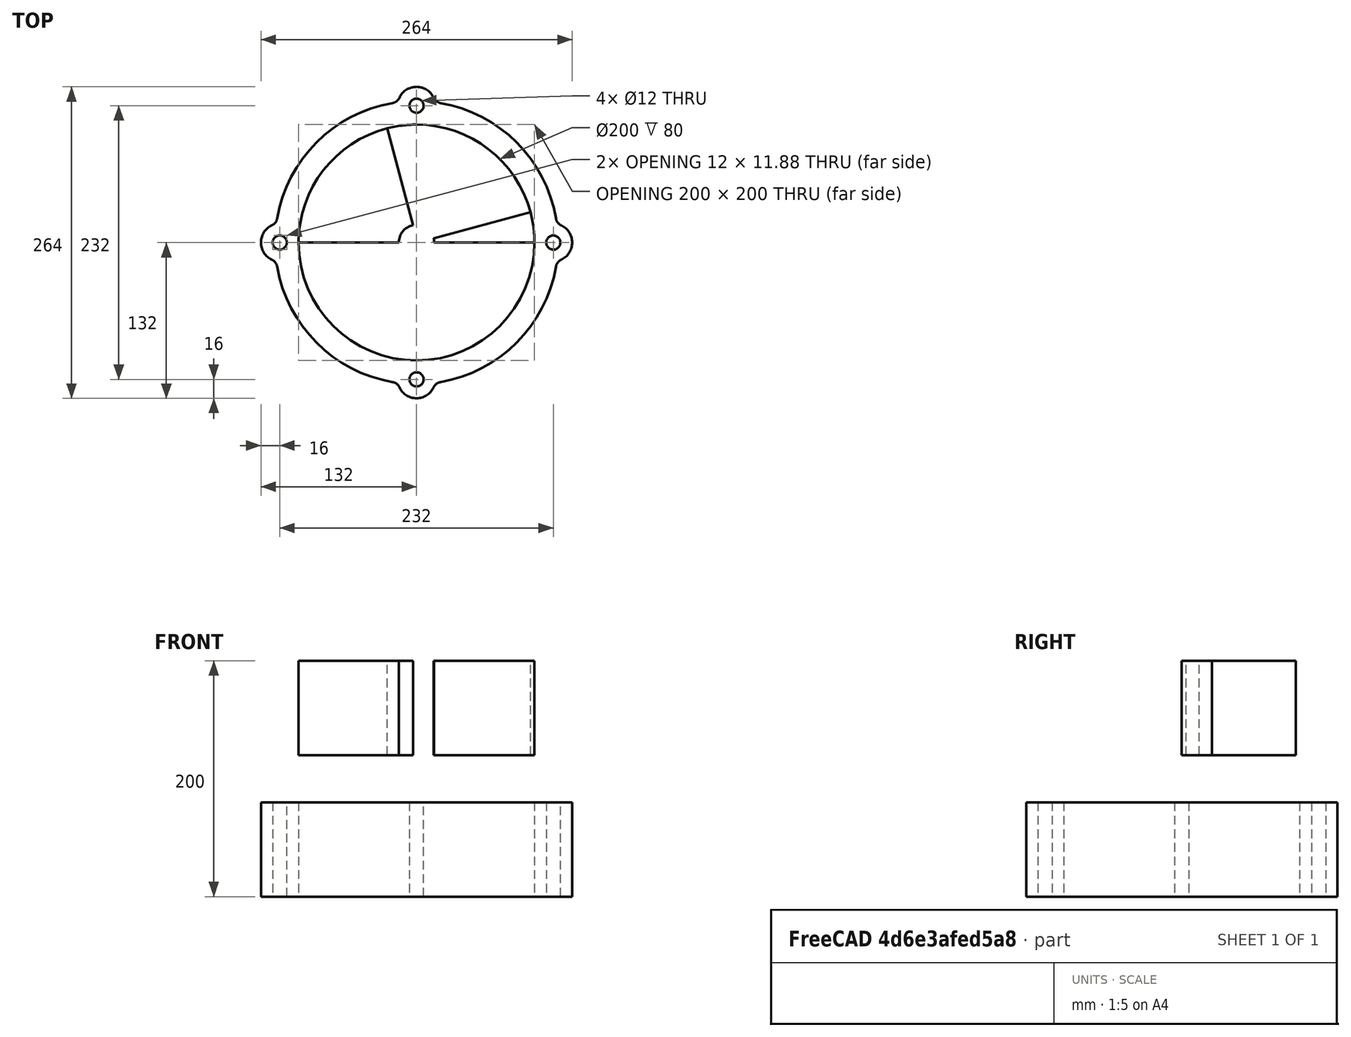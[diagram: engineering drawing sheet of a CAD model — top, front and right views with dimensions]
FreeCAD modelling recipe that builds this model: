
FCSTD DOCUMENT  (FreeCAD 0.20R29410 (Git))
Label: ChamberSolid0
License: All rights reserved
LicenseURL: http://en.wikipedia.org/wiki/All_rights_reserved
objects: Part::Cylinder×10, Part::Cut×7, Part::Fillet×3, Part::FeaturePython×2, Part::Box×2, Part::MultiFuse×1, PartDesign::Body×1
note: 26 computed .brp shape members not serialized (recipe doc carries the construction recipe); baked Part::Feature solids carry a one-line shape summary decoded from their .brp

FEATURE [Part::Cylinder] Cylinder  label="Walec"
  Angle = 360
  AttacherType = Attacher::AttachEngine3D
  FirstAngle = 0
  Height = 80
  Radius = 120
  SecondAngle = 0
FEATURE [Part::Cylinder] Cylinder001  label="Walec001"
  Angle = 360
  AttacherType = Attacher::AttachEngine3D
  FirstAngle = 0
  Height = 200
  Radius = 100
  SecondAngle = 0
FEATURE [Part::Cut] Cut
  Base = -> Cylinder
  Tool = -> Cylinder001
FEATURE [Part::Cylinder] Cylinder002  label="Walec002"
  Angle = 360
  AttacherType = Attacher::AttachEngine3D
  FirstAngle = 0
  Height = 80
  Placement = pos=(116,0,0) rot=(0,0,1;0rad)
  Radius = 16
  SecondAngle = 0
FEATURE [Part::Cylinder] Cylinder003  label="Walec003"
  Angle = 360
  AttacherType = Attacher::AttachEngine3D
  FirstAngle = 0
  Height = 80
  Placement = pos=(-116,0,0) rot=(0,0,1;0rad)
  Radius = 16
  SecondAngle = 0
FEATURE [Part::Cylinder] Cylinder004  label="Walec004"
  Angle = 360
  AttacherType = Attacher::AttachEngine3D
  FirstAngle = 0
  Height = 80
  Placement = pos=(0,116,0) rot=(0,0,1;0rad)
  Radius = 16
  SecondAngle = 0
FEATURE [Part::Cylinder] Cylinder005  label="Walec005"
  Angle = 360
  AttacherType = Attacher::AttachEngine3D
  FirstAngle = 0
  Height = 80
  Placement = pos=(0,-116,0) rot=(0,0,1;0rad)
  Radius = 16
  SecondAngle = 0
FEATURE [Part::Cylinder] Cylinder006  label="Walec006"
  Angle = 360
  AttacherType = Attacher::AttachEngine3D
  FirstAngle = 0
  Height = 80
  Placement = pos=(116,0,0) rot=(0,0,1;0rad)
  Radius = 6
  SecondAngle = 0
FEATURE [Part::Cylinder] Cylinder007  label="Walec007"
  Angle = 360
  AttacherType = Attacher::AttachEngine3D
  FirstAngle = 0
  Height = 80
  Placement = pos=(-116,0,0) rot=(0,0,1;0rad)
  Radius = 6
  SecondAngle = 0
FEATURE [Part::Cylinder] Cylinder008  label="Walec008"
  Angle = 360
  AttacherType = Attacher::AttachEngine3D
  FirstAngle = 0
  Height = 80
  Placement = pos=(0,116,0) rot=(0,0,1;0rad)
  Radius = 6
  SecondAngle = 0
FEATURE [Part::Cylinder] Cylinder009  label="Walec009"
  Angle = 360
  AttacherType = Attacher::AttachEngine3D
  FirstAngle = 0
  Height = 80
  Placement = pos=(0,-116,0) rot=(0,0,1;0rad)
  Radius = 6
  SecondAngle = 0
FEATURE [Part::MultiFuse] Fusion
  Shapes = -> [Cut,Cylinder002,Cylinder003,Cylinder004,Cylinder005]
FEATURE [Part::Cut] Cut001
  Base = -> Fusion
  Tool = -> Cylinder009
FEATURE [Part::Cut] Cut002
  Base = -> Cut001
  Tool = -> Cylinder008
FEATURE [Part::Cut] Cut003
  Base = -> Cut002
  Tool = -> Cylinder007
FEATURE [Part::Cut] Cut004
  Base = -> Cut003
  Tool = -> Cylinder006
FEATURE [Part::FeaturePython] refine  label="refine_Cut004"  # WARN: FeaturePython — macro-defined, semantics opaque (R4)
  Base = -> Cut004
FEATURE [PartDesign::Body] Body
  Origin = -> Origin
FEATURE [Part::Fillet] Fillet
  Base = -> refine
  Edges = 1 edges r=8: [Edge16]
FEATURE [Part::Fillet] Fillet001
  Base = -> Fillet
  Edges = 1 edges r=8: [Edge2]
FEATURE [Part::Fillet] Fillet002
  Base = -> Fillet001
  Edges = 6 edges r=8: [Edge59,Edge60,Edge61,Edge62,Edge63,Edge64]
FEATURE [Part::FeaturePython] Tube  # WARN: FeaturePython — macro-defined, semantics opaque (R4)
  AttacherType = Attacher::AttachEngine3D
  Height = 80
  InnerRadius = 15
  OuterRadius = 100
  Placement = pos=(0,0,120) rot=(0,0,1;0rad)
FEATURE [Part::Box] Box  label="Sześcian"
  AttacherType = Attacher::AttachEngine3D
  Height = 80
  Length = 400
  Placement = pos=(1,0,120) rot=(0,0,1;0.261799rad)
  Width = 200
FEATURE [Part::Box] Box001  label="Sześcian001"
  AttacherType = Attacher::AttachEngine3D
  Height = 80
  Length = 200
  Placement = pos=(-100,-200,120) rot=(0,0,1;0rad)
  Width = 200
FEATURE [Part::Cut] Cut005
  Base = -> Tube
  Tool = -> Box001
FEATURE [Part::Cut] Cut006
  Base = -> Cut005
  Tool = -> Box
